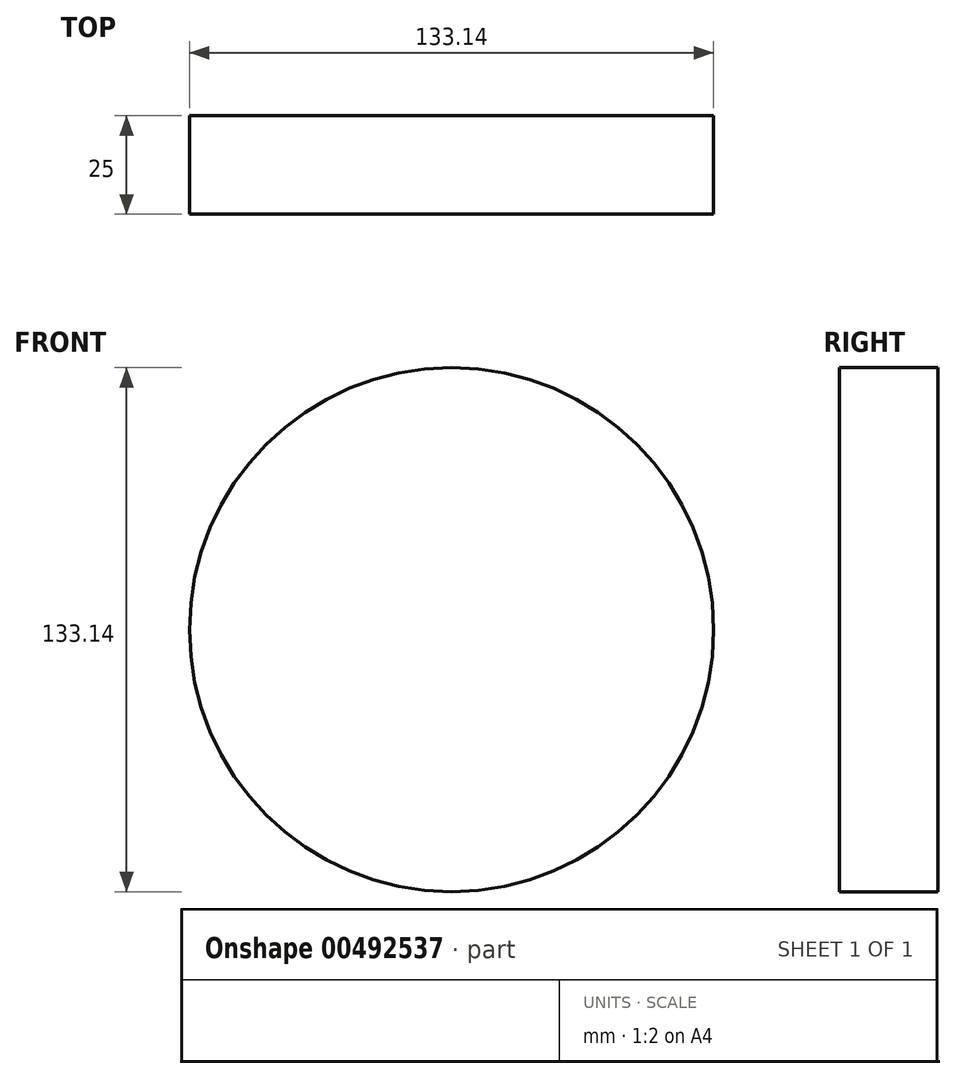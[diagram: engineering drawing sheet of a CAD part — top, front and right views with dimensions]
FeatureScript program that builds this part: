
annotation { "Feature Type Name" : "Feature", "Feature Type Description" : "" }
export const myFeature = defineFeature(function(context is Context, id is Id, definition is map)
    precondition{}
    {
        {
            var Q0;
            Q0=qCreatedBy(makeId("Front.planeOp"),FACE);
            var sketch = newSketch(context, id + "F0", { "sketchPlane" : qUnion([Q0])});
            skCircle(sketch, "E0", {"center": v(0, 0) * mm, "radius": 66.57 * mm});
            skSolve(sketch);
        }
        {
            var Q0;
            Q0=makeQuery(id+"F0.imprint","IMPRINT",FACE,{"disambiguationData":[TD([[makeQuery(id+"F0.imprint","IMPRINT",EDGE,{"derivedFrom":sQuery(id+"F0.wireOp",EDGE,"E0")}),1.0]])]});
            extrude(context, id + "F1", {"entities" : qUnion([Q0]), "depth" : 25 * mm, "offsetDistance" : 25 * mm});
        }
    });
